# Revit family: Kabelrinnen-Systeme_Magic_Bogen 90° Magic_6xx
name_source: partatom
category: Generic Models
revit_build: Autodesk Revit 2015 (Build: 20140606_1530(x64)
units: mm (PartAtom-declared; Revit-internal decimal feet)

## types (14) — shared parameters
Manufacturer = OBO Bettermann
Material = Steel, Galvanized
URL = http://www.obo-bettermann.com

## per-type parameters (varying)
| type | B | GTIN | Manufacturer Art. No. |
| RBM 90 610 FS | 100 mm  [stored 0.328084 ft] | 4012195881810 | 6041130 |
| RBM 90 615 FS | 150 mm | 4012195881827 | 6041132 |
| RBM 90 620 FS | 200 mm  [stored 0.656168 ft] | 4012195881834 | 6041134 |
| RBM 90 630 FS | 300 mm | 4012195881841 | 6041136 |
| RBM 90 640 FS | 400 mm  [stored 1.31234 ft] | 4012195881858 | 6041138 |
| RBM 90 650 FS | 500 mm  [stored 1.64042 ft] | 4012195881865 | 6041140 |
| RBM 90 660 FS | 600 mm | 4012195881872 | 6041142 |
| RBM 90 610 FT | 100 mm  [stored 0.328084 ft] | 4012195881889 | 6041150 |
| RBM 90 615 FT | 150 mm | 4012195881896 | 6041152 |
| RBM 90 620 FT | 200 mm  [stored 0.656168 ft] | 4012195881902 | 6041154 |
| RBM 90 630 FT | 300 mm | 4012195881919 | 6041156 |
| RBM 90 640 FT | 400 mm  [stored 1.31234 ft] | 4012195881926 | 6041158 |
| RBM 90 650 FT | 500 mm  [stored 1.64042 ft] | 4012195881933 | 6041160 |
| RBM 90 660 FT | 600 mm | 4012195881940 | 6041162 |

note: column(s) folded — value = type name in every type: Article Type

note: [stored X ft] marks values corroborated as IEEE doubles in the binary element streams (Revit-internal decimal feet)

## geometry (parser evidence)
native form markers: Sweep x1
no freeform markers — native parametric forms only
